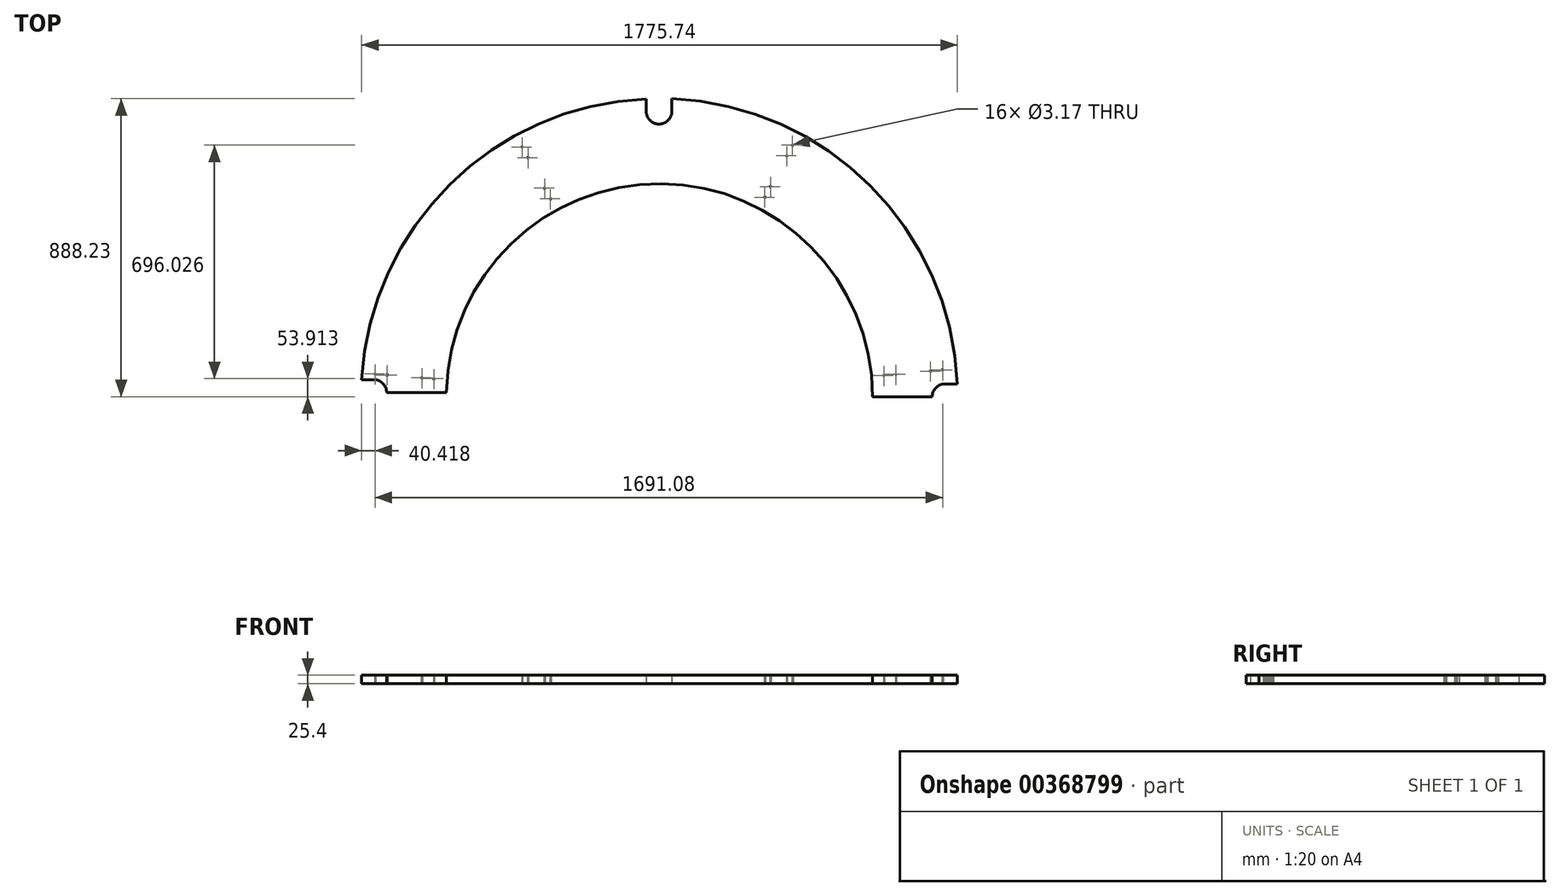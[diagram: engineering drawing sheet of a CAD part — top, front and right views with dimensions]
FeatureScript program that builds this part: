
annotation { "Feature Type Name" : "Feature", "Feature Type Description" : "" }
export const myFeature = defineFeature(function(context is Context, id is Id, definition is map)
    precondition{}
    {
        {
            var Q0;
            Q0=qCreatedBy(makeId("Top.planeOp"),FACE);
            var sketch = newSketch(context, id + "F0", { "sketchPlane" : qUnion([Q0])});
            skArc(sketch, "E0", {"start": v(889.26, 38.1) * mm, "mid": v(629.31, 629) * mm, "end": v(38.1, 888.23) * mm});
            skArc(sketch, "E1", {"start": v(636.07, 0) * mm, "mid": v(7.42, 634.97) * mm, "end": v(-633.8, 12.7) * mm});
            skArc(sketch, "E2", {"start": v(-38.1, 851.18) * mm, "mid": v(-0.14, 812.8) * mm, "end": v(38.1, 850.9) * mm});
            skLineSegment(sketch, "E3", {"start": v(-38.1, 850.9) * mm, "end": v(-37.96, 888.14) * mm});
            skLineSegment(sketch, "E4", {"start": v(38.1, 850.9) * mm, "end": v(38.1, 888.23) * mm});
            skArc(sketch, "E5.trimOffspring", {"start": v(-37.96, 888.14) * mm, "mid": v(-623.37, 632.77) * mm, "end": v(-886.48, 50.8) * mm});
            skPoint(sketch, "E6.orphan", {"position": v(-887.93, 0) * mm});
            skArc(sketch, "E7", {"start": v(851.97, 38.1) * mm, "mid": v(825.03, 26.94) * mm, "end": v(813.87, 0) * mm});
            skLineSegment(sketch, "E8", {"start": v(851.97, 38.1) * mm, "end": v(889.26, 38.1) * mm});
            skLineSegment(sketch, "E9.trimOffspring", {"start": v(813.87, 0) * mm, "end": v(636.07, 0) * mm});
            skPoint(sketch, "E10.orphan", {"position": v(890.07, 0) * mm});
            skCircle(sketch, "E11", {"center": v(-846.06, 67.99) * mm, "radius": 1.59 * mm});
            skCircle(sketch, "E12.1.0", {"center": v(-408.12, 744.23) * mm, "radius": 1.59 * mm});
            skCircle(sketch, "E12.2.0", {"center": v(397.54, 749.94) * mm, "radius": 1.59 * mm});
            skCircle(sketch, "E12.3.0", {"center": v(845.01, 79.96) * mm, "radius": 1.59 * mm});
            skPoint(sketch, "E12.center", {"position": v(0, 0) * mm});
            skCircle(sketch, "E13", {"center": v(-810.21, 65.1) * mm, "radius": 1.59 * mm});
            skCircle(sketch, "E14.1.0", {"center": v(-390.82, 712.7) * mm, "radius": 1.59 * mm});
            skCircle(sketch, "E14.2.0", {"center": v(380.7, 718.16) * mm, "radius": 1.59 * mm});
            skCircle(sketch, "E14.3.0", {"center": v(809.2, 76.57) * mm, "radius": 1.59 * mm});
            skCircle(sketch, "E15", {"center": v(-670.9, 53.91) * mm, "radius": 1.59 * mm});
            skCircle(sketch, "E16", {"center": v(-706.76, 56.8) * mm, "radius": 1.59 * mm});
            skCircle(sketch, "E17.1.0", {"center": v(-340.92, 621.7) * mm, "radius": 1.59 * mm});
            skCircle(sketch, "E17.2.0", {"center": v(332.08, 626.46) * mm, "radius": 1.59 * mm});
            skCircle(sketch, "E17.3.0", {"center": v(705.89, 66.8) * mm, "radius": 1.59 * mm});
            skCircle(sketch, "E18.1.0", {"center": v(-323.63, 590.16) * mm, "radius": 1.59 * mm});
            skCircle(sketch, "E18.2.0", {"center": v(315.24, 594.69) * mm, "radius": 1.59 * mm});
            skCircle(sketch, "E18.3.0", {"center": v(670.08, 63.4) * mm, "radius": 1.59 * mm});
            skLineSegment(sketch, "E19", {"start": v(-886.48, 50.8) * mm, "end": v(-849.83, 50.8) * mm});
            skPoint(sketch, "E20.visualSharp", {"position": v(-811.73, 50.8) * mm});
            skArc(sketch, "E20.filletArc", {"start": v(-811.73, 12.7) * mm, "mid": v(-822.89, 39.64) * mm, "end": v(-849.83, 50.8) * mm});
            skLineSegment(sketch, "E21", {"start": v(-811.73, 12.7) * mm, "end": v(-633.8, 12.7) * mm});
            skSolve(sketch);
        }
        {
            var Q0;
            Q0=makeQuery(id+"F0.imprint","IMPRINT",FACE,{"disambiguationData":[TD([[makeQuery(id+"F0.imprint","IMPRINT",EDGE,{"derivedFrom":sQuery(id+"F0.wireOp",EDGE,"E0")}),1.0]])]});
            extrude(context, id + "F1", {"entities" : qUnion([Q0]), "depth" : 25.4 * mm});
        }
    });
